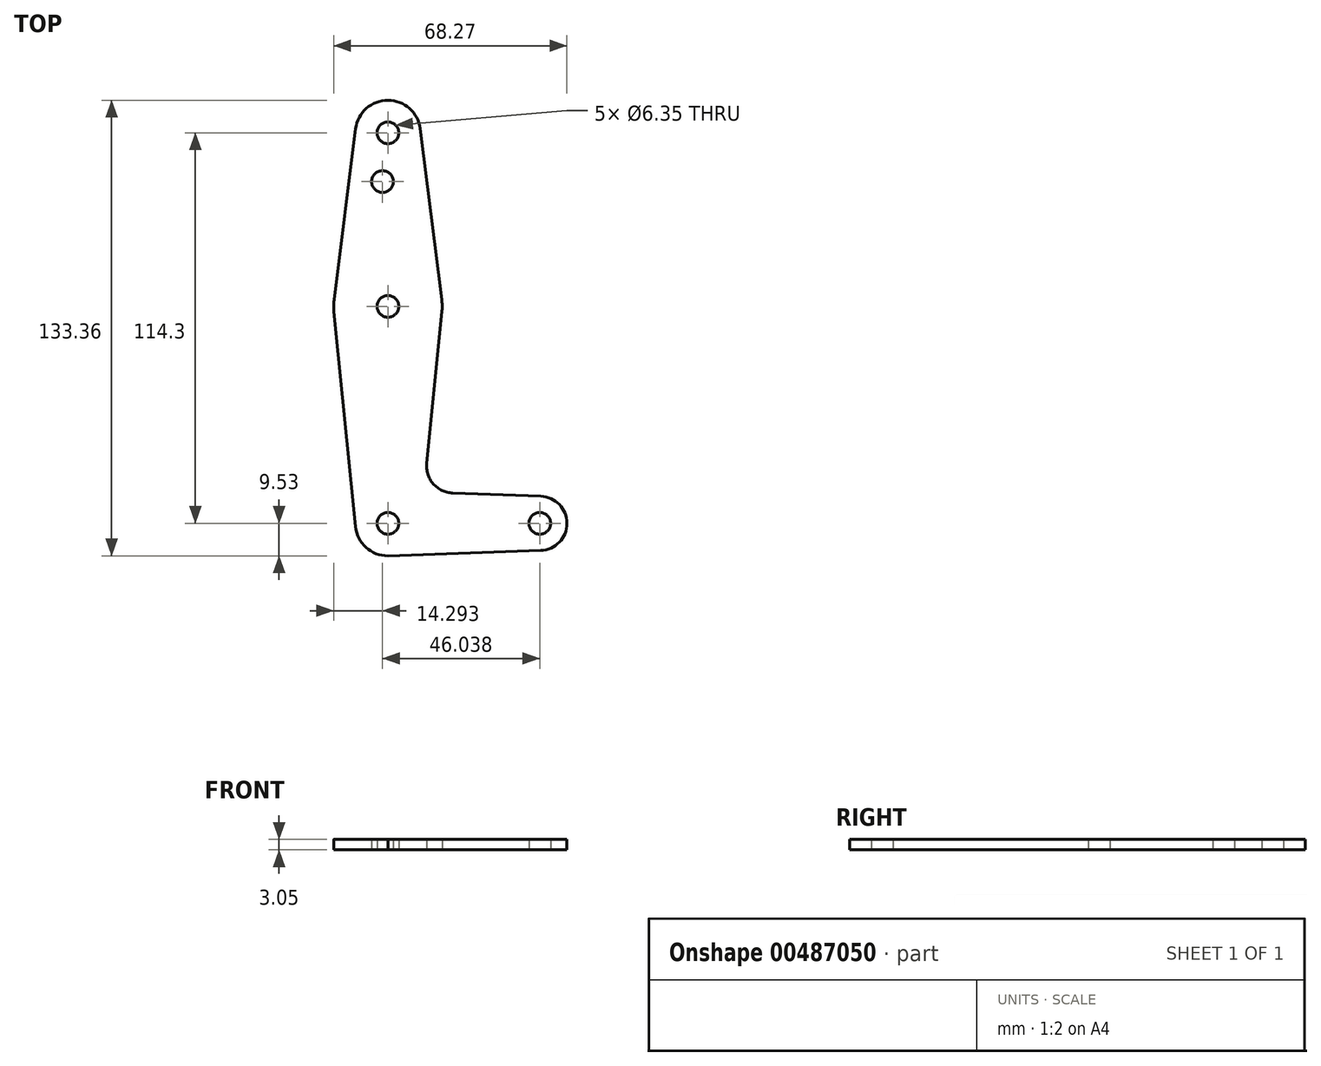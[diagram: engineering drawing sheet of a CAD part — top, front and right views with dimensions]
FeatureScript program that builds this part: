
annotation { "Feature Type Name" : "Feature", "Feature Type Description" : "" }
export const myFeature = defineFeature(function(context is Context, id is Id, definition is map)
    precondition{}
    {
        {
            var Q0;
            Q0=qCreatedBy(makeId("Top.planeOp"),FACE);
            var sketch = newSketch(context, id + "F0", { "sketchPlane" : qUnion([Q0])});
            skLineSegment(sketch, "E0", {"start": v(0, 0) * mm, "end": v(0, 114.3) * mm, "construction": true});
            skLineSegment(sketch, "E1", {"start": v(0, 0) * mm, "end": v(44.45, 0) * mm, "construction": true});
            skCircle(sketch, "E2", {"center": v(0, 0) * mm, "radius": 9.53 * mm});
            skCircle(sketch, "E3", {"center": v(44.45, 0) * mm, "radius": 7.94 * mm});
            skCircle(sketch, "E4", {"center": v(0, 63.5) * mm, "radius": 15.88 * mm});
            skCircle(sketch, "E5", {"center": v(0, 114.3) * mm, "radius": 9.53 * mm});
            skLineSegment(sketch, "E6", {"start": v(9.45, 115.5) * mm, "end": v(15.75, 65.48) * mm});
            skLineSegment(sketch, "E7", {"start": v(-9.45, 115.5) * mm, "end": v(-15.75, 65.48) * mm});
            skLineSegment(sketch, "E8", {"start": v(15.8, 61.91) * mm, "end": v(11.34, 17.59) * mm});
            skLineSegment(sketch, "E9", {"start": v(-15.8, 61.91) * mm, "end": v(-9.48, -0.95) * mm});
            skLineSegment(sketch, "E10", {"start": v(18.97, 8.85) * mm, "end": v(44.73, 7.93) * mm});
            skLineSegment(sketch, "E11", {"start": v(0, -9.53) * mm, "end": v(44.73, -7.93) * mm});
            skCircle(sketch, "E12", {"center": v(0, 114.3) * mm, "radius": 3.18 * mm});
            skCircle(sketch, "E13", {"center": v(0, 0) * mm, "radius": 3.18 * mm});
            skCircle(sketch, "E14", {"center": v(44.45, 0) * mm, "radius": 3.18 * mm});
            skCircle(sketch, "E15", {"center": v(-1.59, 100.03) * mm, "radius": 3.18 * mm});
            skCircle(sketch, "E16", {"center": v(0, 63.5) * mm, "radius": 3.18 * mm});
            skArc(sketch, "E17.filletArc", {"start": v(11.34, 17.59) * mm, "mid": v(13.26, 11.57) * mm, "end": v(18.97, 8.85) * mm});
            skSolve(sketch);
        }
        {
            var Q0;
            Q0=makeQuery(id+"F0.imprint","IMPRINT",FACE,{"disambiguationData":[TD([[makeQuery(id+"F0.imprint","IMPRINT",EDGE,{"derivedFrom":sQuery(id+"F0.wireOp",EDGE,"E12")}),-1.0]])]});
            var Q1;
            {var subQ1=sQuery(id+"F0.wireOp",EDGE,"E6");Q1=makeQuery(id+"F0.imprint","IMPRINT",FACE,{"disambiguationData":[TD([[makeQuery(id+"F0.imprint","IMPRINT",EDGE,{"derivedFrom":subQ1}),-1.0]])]});}
            var Q2;
            Q2=makeQuery(id+"F0.imprint","IMPRINT",FACE,{"disambiguationData":[TD([[makeQuery(id+"F0.imprint","IMPRINT",EDGE,{"derivedFrom":sQuery(id+"F0.wireOp",EDGE,"E16")}),-1.0]])]});
            var Q3;
            {var subQ0=sQuery(id+"F0.wireOp",EDGE,"E8");Q3=makeQuery(id+"F0.imprint","IMPRINT",FACE,{"disambiguationData":[TD([[makeQuery(id+"F0.imprint","IMPRINT",EDGE,{"derivedFrom":subQ0}),-1.0]])]});}
            var Q4;
            Q4=makeQuery(id+"F0.imprint","IMPRINT",FACE,{"disambiguationData":[TD([[makeQuery(id+"F0.imprint","IMPRINT",EDGE,{"derivedFrom":sQuery(id+"F0.wireOp",EDGE,"E13")}),-1.0]])]});
            var Q5;
            Q5=makeQuery(id+"F0.imprint","IMPRINT",FACE,{"disambiguationData":[TD([[makeQuery(id+"F0.imprint","IMPRINT",EDGE,{"derivedFrom":sQuery(id+"F0.wireOp",EDGE,"E14")}),-1.0]])]});
            extrude(context, id + "F1", {"entities" : qUnion([Q0, Q1, Q2, Q3, Q4, Q5]), "depth" : 3.05 * mm});
        }
    });
